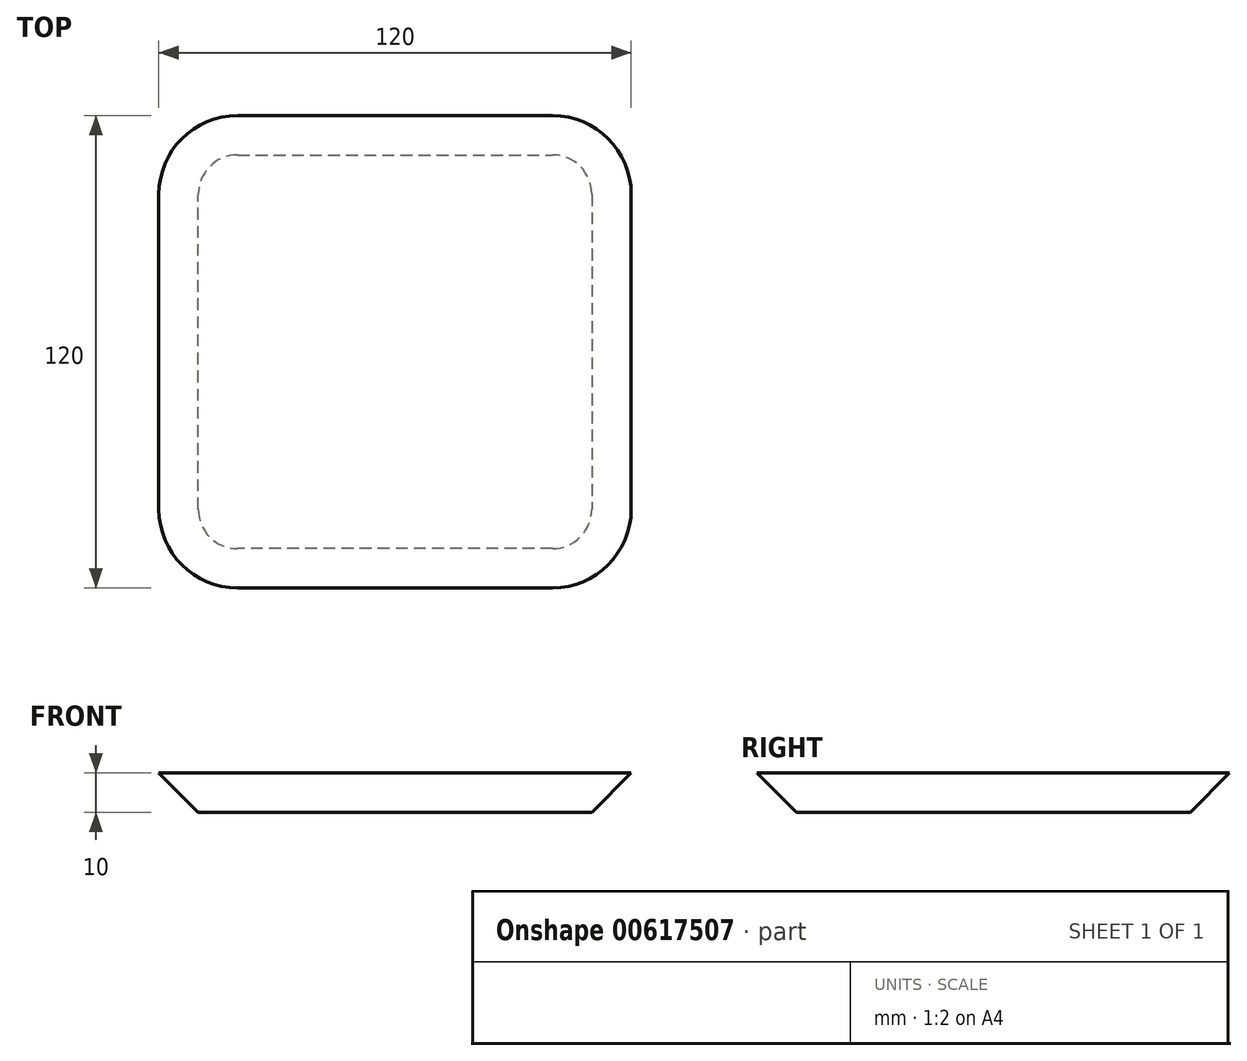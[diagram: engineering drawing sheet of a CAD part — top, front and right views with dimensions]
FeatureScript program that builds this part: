
annotation { "Feature Type Name" : "Feature", "Feature Type Description" : "" }
export const myFeature = defineFeature(function(context is Context, id is Id, definition is map)
    precondition{}
    {
        {
            var Q0;
            Q0=qCreatedBy(makeId("Top.planeOp"),FACE);
            var sketch = newSketch(context, id + "F0", { "sketchPlane" : qUnion([Q0])});
            skLineSegment(sketch, "E0.bottom", {"start": v(40, -60) * mm, "end": v(-40, -60) * mm});
            skLineSegment(sketch, "E0.top", {"start": v(40, 60) * mm, "end": v(-40, 60) * mm});
            skLineSegment(sketch, "E0.left", {"start": v(60, -40) * mm, "end": v(60, 40) * mm});
            skLineSegment(sketch, "E0.right", {"start": v(-60, -40) * mm, "end": v(-60, 40) * mm});
            skPoint(sketch, "E0.middle", {"position": v(0, 0) * mm});
            skPoint(sketch, "E1.visualSharp", {"position": v(-60, 60) * mm});
            skArc(sketch, "E1.filletArc", {"start": v(-40, 60) * mm, "mid": v(-54.14, 54.14) * mm, "end": v(-60, 40) * mm});
            skPoint(sketch, "E2.visualSharp", {"position": v(-60, -60) * mm});
            skArc(sketch, "E2.filletArc", {"start": v(-60, -40) * mm, "mid": v(-54.14, -54.14) * mm, "end": v(-40, -60) * mm});
            skPoint(sketch, "E3.visualSharp", {"position": v(60, 60) * mm});
            skArc(sketch, "E3.filletArc", {"start": v(60, 40) * mm, "mid": v(54.14, 54.14) * mm, "end": v(40, 60) * mm});
            skPoint(sketch, "E4.visualSharp", {"position": v(60, -60) * mm});
            skArc(sketch, "E4.filletArc", {"start": v(40, -60) * mm, "mid": v(54.14, -54.14) * mm, "end": v(60, -40) * mm});
            skSolve(sketch);
        }
        {
            var Q0;
            Q0=makeQuery(id+"F0.imprint","IMPRINT",FACE,{"disambiguationData":[TD([[makeQuery(id+"F0.imprint","IMPRINT",EDGE,{"derivedFrom":sQuery(id+"F0.wireOp",EDGE,"E0.bottom")}),-1.0]])]});
            extrude(context, id + "F1", {"entities" : qUnion([Q0]), "depth" : 10 * mm, "offsetDistance" : 25 * mm});
        }
        {
            var Q0;
            Q0=makeQuery(id+"F1.opExtrude","CAP_EDGE",EDGE,{"disambiguationData":[OSD([sQuery(id+"F0.wireOp",EDGE,"E0.right")])],"isStart":true});
            chamfer(context, id + "F2", {"entities" : qUnion([Q0]), "width" : 10 * mm, "tangentPropagation" : true});
        }
    });
